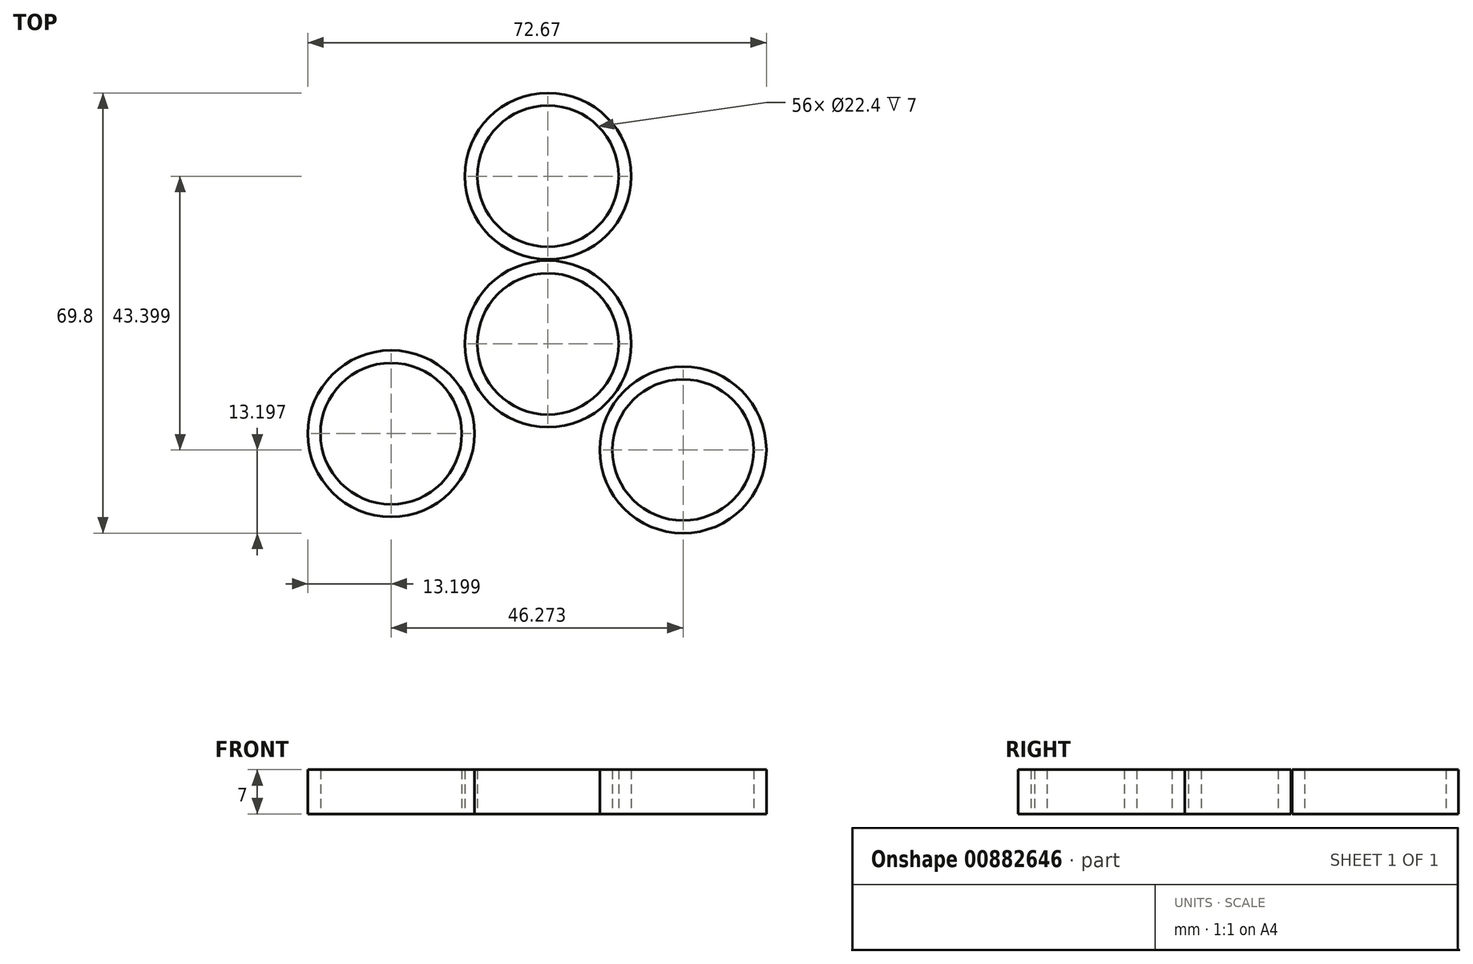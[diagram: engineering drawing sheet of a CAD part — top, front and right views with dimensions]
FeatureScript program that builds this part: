
annotation { "Feature Type Name" : "Feature", "Feature Type Description" : "" }
export const myFeature = defineFeature(function(context is Context, id is Id, definition is map)
    precondition{}
    {
        {
            var Q0;
            Q0=qCreatedBy(makeId("Top.planeOp"),FACE);
            var sketch = newSketch(context, id + "F0", { "sketchPlane" : qUnion([Q0])});
            skCircle(sketch, "E0", {"center": v(0, 0) * mm, "radius": 13.2 * mm});
            skCircle(sketch, "E1", {"center": v(0, 0) * mm, "radius": 11.2 * mm});
            skCircle(sketch, "E2", {"center": v(-24.86, -14.23) * mm, "radius": 13.2 * mm});
            skCircle(sketch, "E3", {"center": v(-24.86, -14.23) * mm, "radius": 11.2 * mm});
            skCircle(sketch, "E4", {"center": v(21.41, -16.81) * mm, "radius": 13.2 * mm});
            skCircle(sketch, "E5", {"center": v(21.41, -16.81) * mm, "radius": 11.2 * mm});
            skCircle(sketch, "E6", {"center": v(0, 26.59) * mm, "radius": 13.2 * mm});
            skCircle(sketch, "E7", {"center": v(0, 26.59) * mm, "radius": 11.2 * mm});
            skSolve(sketch);
        }
        {
            var Q0;
            Q0 = qSketchRegion(id + "F0", true);
            extrude(context, id + "F1", {"entities" : qUnion([Q0]), "depth" : 7 * mm, "offsetDistance" : 25 * mm});
        }
    });
